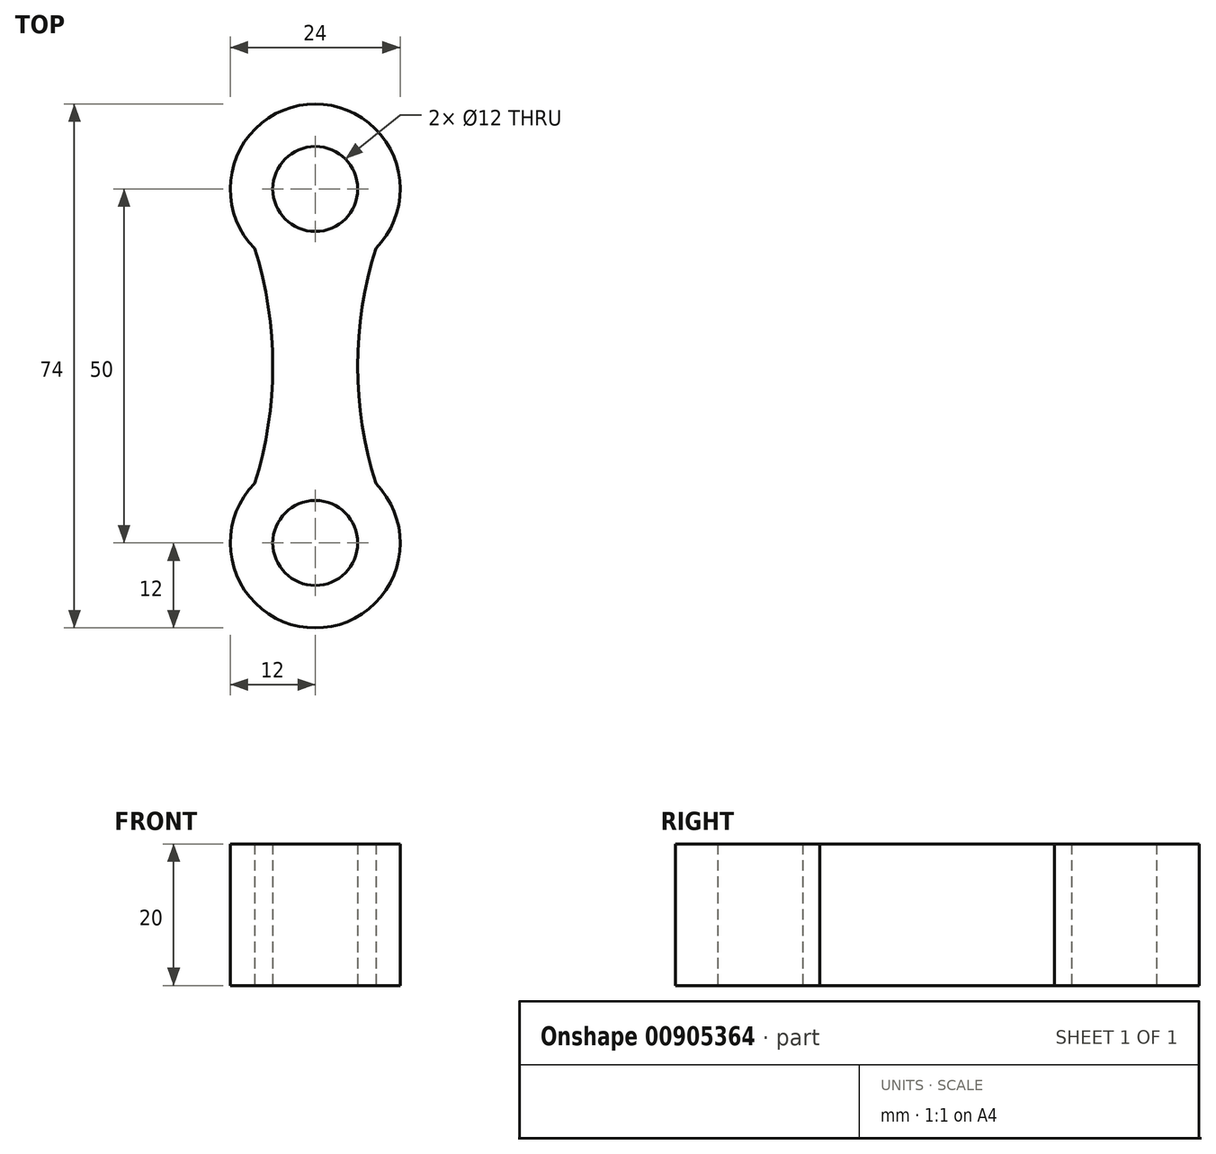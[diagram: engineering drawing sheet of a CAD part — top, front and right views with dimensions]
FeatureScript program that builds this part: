
annotation { "Feature Type Name" : "Feature", "Feature Type Description" : "" }
export const myFeature = defineFeature(function(context is Context, id is Id, definition is map)
    precondition{}
    {
        {
            var Q0;
            Q0=qCreatedBy(makeId("Top.planeOp"),FACE);
            var sketch = newSketch(context, id + "F0", { "sketchPlane" : qUnion([Q0])});
            skCircle(sketch, "E0", {"center": v(0, 50) * mm, "radius": 6 * mm});
            skCircle(sketch, "E1", {"center": v(0, 0) * mm, "radius": 6 * mm});
            skArc(sketch, "E2", {"start": v(8.56, 41.59) * mm, "mid": v(0, 62) * mm, "end": v(-8.56, 41.59) * mm});
            skArc(sketch, "E3", {"start": v(-8.56, 8.41) * mm, "mid": v(0, -12) * mm, "end": v(8.56, 8.41) * mm});
            skLineSegment(sketch, "E4", {"start": v(0, 0) * mm, "end": v(0, 6) * mm});
            skArc(sketch, "E5", {"start": v(-8.56, 8.41) * mm, "mid": v(-6, 25) * mm, "end": v(-8.56, 41.59) * mm});
            skArc(sketch, "E6", {"start": v(8.56, 41.59) * mm, "mid": v(6, 25) * mm, "end": v(8.56, 8.41) * mm});
            skPoint(sketch, "E7.start.orphan", {"position": v(-20.36, 50) * mm});
            skPoint(sketch, "E8.orphan", {"position": v(-12, 0) * mm});
            skPoint(sketch, "E9.orphan", {"position": v(12, 0) * mm});
            skPoint(sketch, "E10.end.orphan", {"position": v(6, 25) * mm});
            skPoint(sketch, "E11.orphan", {"position": v(0, 25) * mm});
            skPoint(sketch, "E12.start.orphan", {"position": v(-20.36, 0) * mm});
            skSolve(sketch);
        }
        {
            var Q0;
            Q0 = qSketchRegion(id + "F0", true);
            extrude(context, id + "F1", {"entities" : qUnion([Q0]), "depth" : 20 * mm, "offsetDistance" : 25 * mm});
        }
    });
